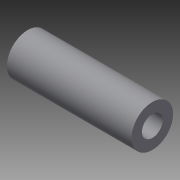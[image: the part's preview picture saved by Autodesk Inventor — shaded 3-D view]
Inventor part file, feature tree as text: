
AUTODESK INVENTOR PART (.ipt)
format: ipt  version: 2015 (Build 190159000, 159)  size: 77,312 bytes
history: native  units: in
note: dims shown in document units (in); Inventor stores cm internally (conversion verified against a paired STEP export)
features: extrude x1, sketch x1
ambient origin geometry x8: Origin, YZ Plane, XZ Plane, XY Plane, X Axis, Y Axis, Z Axis, Center Point
bodies: Solid1 (feature_tree)
feature tree (2):
  extrude  "Extrusion1"  Depth=1.0in
  sketch  "Sketch1"  dims[d0=2.0in d1=1.0in d2=6.0in d3=0.0in]
